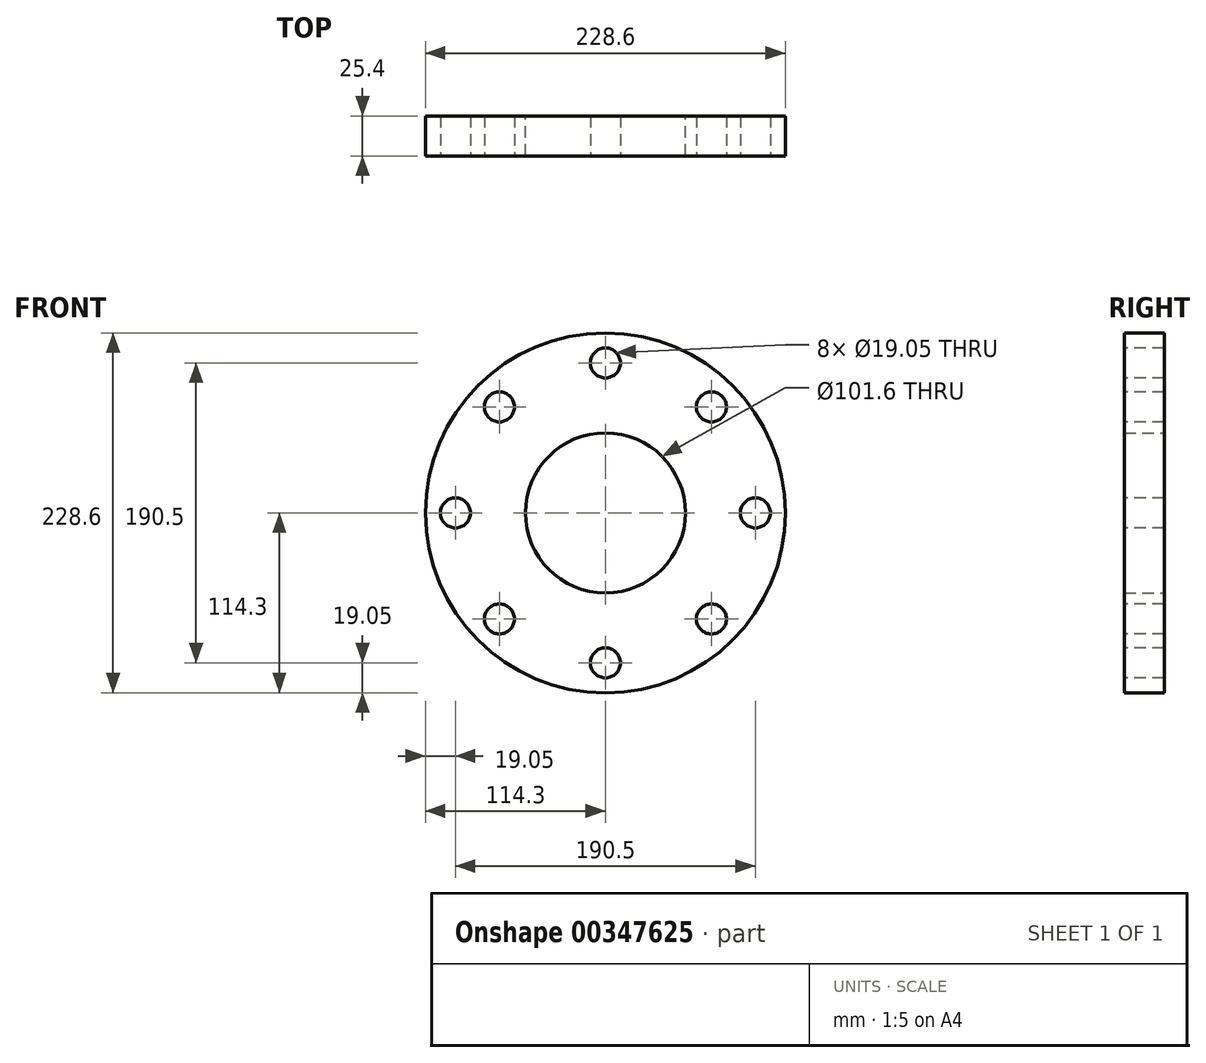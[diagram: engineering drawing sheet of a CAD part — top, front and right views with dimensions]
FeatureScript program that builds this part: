
annotation { "Feature Type Name" : "Feature", "Feature Type Description" : "" }
export const myFeature = defineFeature(function(context is Context, id is Id, definition is map)
    precondition{}
    {
        {
            var Q0;
            Q0=qCreatedBy(makeId("Front.planeOp"),FACE);
            var sketch = newSketch(context, id + "F0", { "sketchPlane" : qUnion([Q0])});
            skCircle(sketch, "E0", {"center": v(0, 0) * mm, "radius": 114.3 * mm});
            skCircle(sketch, "E1", {"center": v(0, 0) * mm, "radius": 50.8 * mm});
            skSolve(sketch);
        }
        {
            var Q0;
            Q0=makeQuery(id+"F0.imprint","IMPRINT",FACE,{"disambiguationData":[TD([[makeQuery(id+"F0.imprint","IMPRINT",EDGE,{"derivedFrom":sQuery(id+"F0.wireOp",EDGE,"E0")}),1.0]])]});
            extrude(context, id + "F1", {"entities" : qUnion([Q0]), "depth" : 25.4 * mm});
        }
        {
            var Q0;
            Q0=makeQuery(id+"F1.opExtrude","CAP_FACE",FACE,{"disambiguationData":[OSD([sQuery(id+"F0.wireOp",EDGE,"E0"),sQuery(id+"F0.wireOp",EDGE,"E1")])],"isStart":false});
            var sketch = newSketch(context, id + "F2", { "sketchPlane" : qUnion([Q0])});
            skCircle(sketch, "E2", {"center": v(0, 95.25) * mm, "radius": 9.53 * mm});
            skLineSegment(sketch, "E3", {"start": v(0, 0) * mm, "end": v(0, 189.27) * mm, "construction": true});
            skCircle(sketch, "E4.1.0", {"center": v(-67.35, 67.35) * mm, "radius": 9.53 * mm});
            skCircle(sketch, "E4.2.0", {"center": v(-95.25, 0) * mm, "radius": 9.53 * mm});
            skCircle(sketch, "E4.3.0", {"center": v(-67.35, -67.35) * mm, "radius": 9.53 * mm});
            skCircle(sketch, "E4.4.0", {"center": v(0, -95.25) * mm, "radius": 9.53 * mm});
            skCircle(sketch, "E4.5.0", {"center": v(67.35, -67.35) * mm, "radius": 9.53 * mm});
            skCircle(sketch, "E4.6.0", {"center": v(95.25, 0) * mm, "radius": 9.53 * mm});
            skCircle(sketch, "E4.7.0", {"center": v(67.35, 67.35) * mm, "radius": 9.53 * mm});
            skPoint(sketch, "E4.center", {"position": v(0, 0) * mm});
            skSolve(sketch);
        }
        {
            var Q0;
            Q0 = qSketchRegion(id + "F2", true);
            var Q1;
            Q1=makeQuery(id+"F1.opExtrude","CAP_FACE",FACE,{"disambiguationData":[OSD([sQuery(id+"F0.wireOp",EDGE,"E0"),sQuery(id+"F0.wireOp",EDGE,"E1")])],"isStart":true});
            extrude(context, id + "F3", {"entities" : qUnion([Q0]), "operationType" : NewBodyOperationType.REMOVE, "endBound" : BoundingType.UP_TO_SURFACE, "oppositeDirection" : true, "endBoundEntityFace" : qUnion([Q1]), "depth" : 25.4 * mm});
        }
    });
